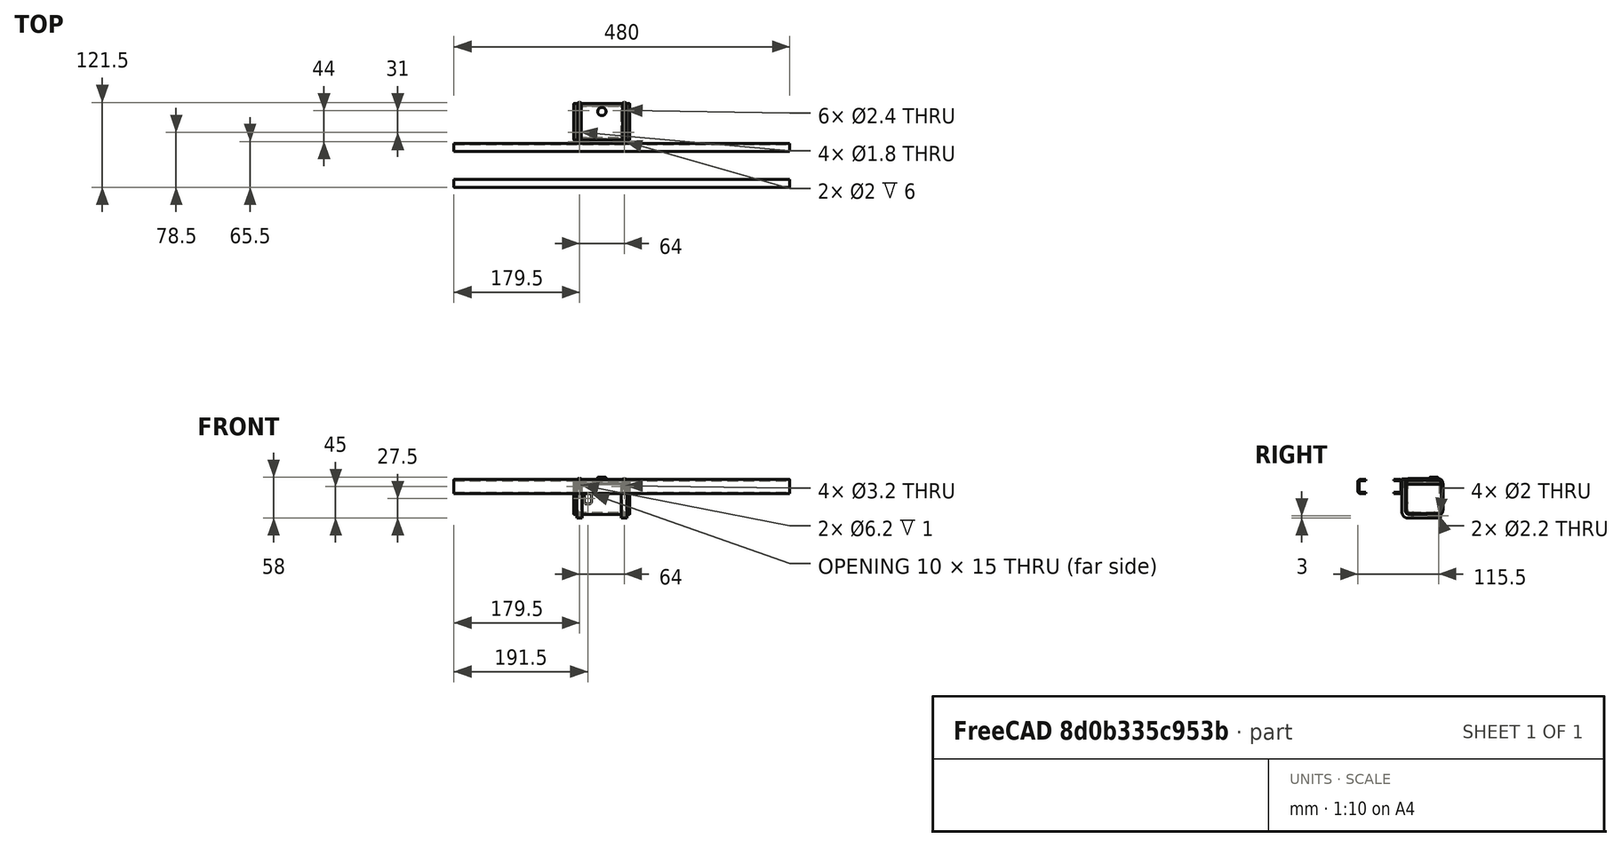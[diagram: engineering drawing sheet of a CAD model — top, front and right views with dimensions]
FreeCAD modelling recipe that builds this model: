
FCSTD DOCUMENT  (FreeCAD 0.16R5602 (Git))
Label: fuel-tank
License: All rights reserved
LicenseURL: http://en.wikipedia.org/wiki/All_rights_reserved
objects: Part::Box×35, Part::Cylinder×30, Part::Cut×27, Part::Fillet×26, Part::MultiFuse×19, Part::Chamfer×5, Part::Mirroring×1
note: 143 computed .brp shape members not serialized (recipe doc carries the construction recipe); baked Part::Feature solids carry a one-line shape summary decoded from their .brp

FEATURE [Part::Box] Box416  label="Cube641"
  Height = 20
  Length = 480
  Placement = pos=(0,0,-92) rot=(0,0,1;0rad)
  Width = 11.5
FEATURE [Part::Box] Box417  label="Cube642"
  Height = 17
  Length = 480
  Placement = pos=(0,1.5,-90.5) rot=(0,0,1;0rad)
  Width = 10
FEATURE [Part::Cut] Cut429  label="Cut769"
  Base = -> Box416
  Tool = -> Box417
FEATURE [Part::Fillet] Fillet268
  Base = -> Cut429
  Edges = 2 edges r=3: [Edge11,Edge23]
  Placement = pos=(0,-1.5,0) rot=(0,0,1;0rad)
FEATURE [Part::Box] Box418  label="Cube643"
  Height = 20
  Length = 480
  Placement = pos=(0,0,-92) rot=(0,0,1;0rad)
  Width = 11.5
FEATURE [Part::Box] Box419  label="Cube644"
  Height = 17
  Length = 480
  Placement = pos=(0,1.5,-90.5) rot=(0,0,1;0rad)
  Width = 10
FEATURE [Part::Cut] Cut430  label="Cut770"
  Base = -> Box418
  Tool = -> Box419
FEATURE [Part::Fillet] Fillet269
  Base = -> Cut430
  Edges = 2 edges r=3: [Edge11,Edge23]
FEATURE [Part::Mirroring] Part__Mirroring036  label="Fillet269 (Mirror #29)"
  Base = (0,0,0)
  Normal = (0,1,0)
  Placement = pos=(0,61.5,0) rot=(0,0,1;0rad)
  Source = -> Fillet269
FEATURE [Part::MultiFuse] Fusion231  label="frame-00"
  Placement = pos=(23.5,55,74) rot=(0,0,1;0rad)
  Shapes = -> [Part__Mirroring036,Fillet268]
FEATURE [Part::Box] Box517  label="Cube719"
  Height = 49
  Length = 0.5
  Placement = pos=(195,122,-50.5) rot=(0,0,1;0rad)
  Width = 51
FEATURE [Part::Fillet] Fillet372
  Base = -> Box517
  Edges = 4 edges r=6: [Edge9,Edge10,Edge11,Edge12]
FEATURE [Part::Cylinder] Cylinder950  label="Cylinder1002"
  Angle = 360
  Height = 2
  Placement = pos=(235,162,0) rot=(0,0,1;0rad)
  Radius = 6
FEATURE [Part::Cylinder] Cylinder951  label="Cylinder1003"
  Angle = 360
  Height = 3
  Placement = pos=(235,162,-1) rot=(0,0,1;0rad)
  Radius = 5
FEATURE [Part::MultiFuse] Fusion605
  Shapes = -> [Cylinder950,Cylinder951]
FEATURE [Part::Fillet] Fillet373
  Base = -> Fusion605
  Edges = 2 edges r=0.5: [Edge1,Edge3]
FEATURE [Part::Chamfer] Chamfer109
  Base = -> Fillet373
  Edges = 1 edges r=0.49: [Edge8]
FEATURE [Part::Box] Box518  label="Cube720"
  Height = 50
  Length = 80
  Placement = pos=(195,121.5,-51) rot=(0,0,1;0rad)
  Width = 52
FEATURE [Part::Fillet] Fillet374
  Base = -> Box518
  Edges = 4 edges r=6: [Edge9,Edge10,Edge11,Edge12]
FEATURE [Part::Box] Box519  label="Cube721"
  Height = 49
  Length = 0.5
  Placement = pos=(195,122,-50.5) rot=(0,0,1;0rad)
  Width = 51
FEATURE [Part::Fillet] Fillet375
  Base = -> Box519
  Edges = 4 edges r=6: [Edge9,Edge10,Edge11,Edge12]
  Placement = pos=(79.5,0,0) rot=(0,0,1;0rad)
FEATURE [Part::MultiFuse] Fusion606
  Shapes = -> [Chamfer109,Fillet374]
FEATURE [Part::MultiFuse] Fusion607
  Shapes = -> [Fillet375,Fillet372]
FEATURE [Part::Cut] Cut014115  label="Cut014173"
  Base = -> Fusion606
  Tool = -> Fusion607
FEATURE [Part::Chamfer] Chamfer110
  Base = -> Cut014115
  Edges = 2 edges r=0.49: [Edge59,Edge78]
FEATURE [Part::Fillet] Fillet376  label="_tank-00"
  Base = -> Chamfer110
  Edges = 2 edges r=0.49: [Edge15,Edge48]
FEATURE [Part::Box] Box523  label="Cube724"
  Height = 5
  Length = 8
  Placement = pos=(199,116.5,-53) rot=(0,0,1;0rad)
  Width = 55
FEATURE [Part::Box] Box527  label="Cube728"
  Height = 4
  Length = 5.5
  Placement = pos=(200.25,165.5,-52) rot=(0,0,1;0rad)
  Width = 6
FEATURE [Part::Cylinder] Cylinder954  label="Cylinder1006"
  Angle = 360
  Height = 8
  Placement = pos=(199,169,-50) rot=(0,1,0;1.5708rad)
  Radius = 1
FEATURE [Part::Box] Box539  label="Cube740"
  Height = 50
  Length = 8
  Placement = pos=(199,116.5,-48) rot=(0,0,1;0rad)
  Width = 5
FEATURE [Part::Box] Box540  label="Cube741"
  Height = 2.5
  Length = 5.5
  Placement = pos=(200.25,116.5,-0.5) rot=(0,0,1;0rad)
  Width = 5
FEATURE [Part::Cylinder] Cylinder962  label="Cylinder1013"
  Angle = 360
  Height = 10
  Placement = pos=(203,119,-6.5) rot=(0,0,1;0rad)
  Radius = 1
FEATURE [Part::Box] Box541  label="Cube742"
  Height = 44
  Length = 74
  Placement = pos=(198,124.5,-48) rot=(0,0,1;0rad)
  Width = 46
FEATURE [Part::Cylinder] Cylinder964  label="Cylinder1015"
  Angle = 360
  Height = 15
  Placement = pos=(203,123,-8) rot=(1,0,0;1.5708rad)
  Radius = 1.6
FEATURE [Part::Cylinder] Cylinder965  label="Cylinder1016"
  Angle = 360
  Height = 15
  Placement = pos=(267,123,-8) rot=(1,0,0;1.5708rad)
  Radius = 1.6
FEATURE [Part::Cylinder] Cylinder966  label="Cylinder1017"
  Angle = 360
  Height = 2
  Placement = pos=(203,123,-8) rot=(1,0,0;1.5708rad)
  Radius = 3.1
FEATURE [Part::Cylinder] Cylinder967  label="Cylinder1018"
  Angle = 360
  Height = 2
  Placement = pos=(267,123,-8) rot=(1,0,0;1.5708rad)
  Radius = 3.1
FEATURE [Part::MultiFuse] Fusion624
  Placement = pos=(0,2.5,0) rot=(0,0,1;0rad)
  Shapes = -> [Cylinder964,Cylinder966,Cylinder967,Cylinder965]
FEATURE [Part::Box] Box554  label="Cube755"
  Height = 15
  Length = 10
  Placement = pos=(210,118.5,-33) rot=(0,0,1;0rad)
  Width = 5
FEATURE [Part::Fillet] Fillet388
  Base = -> Box554
  Edges = 4 edges r=3: [Edge2,Edge4,Edge6,Edge8]
  Placement = pos=(0,1,0) rot=(0,0,1;0rad)
FEATURE [Part::Box] Box558  label="Cube759"
  Height = 44
  Length = 80
  Placement = pos=(195,121.5,-52) rot=(0,0,1;0rad)
  Width = 52
FEATURE [Part::Box] Box559  label="Cube760"
  Height = 10
  Length = 80
  Placement = pos=(195,121.5,-8) rot=(0,0,1;0rad)
  Width = 52
FEATURE [Part::Fillet] Fillet
  Base = -> Box541
  Edges = 4 edges r=4: [Edge9,Edge10,Edge11,Edge12]
FEATURE [Part::Cut] Cut  label="tank-lower"
  Base = -> Fillet376
  Tool = -> Fillet
FEATURE [Part::Box] Box560  label="Cube761"
  Height = 49
  Length = 0.5
  Placement = pos=(195,122,-50.5) rot=(0,0,1;0rad)
  Width = 51
FEATURE [Part::Fillet] Fillet390
  Base = -> Box560
  Edges = 4 edges r=6: [Edge9,Edge10,Edge11,Edge12]
FEATURE [Part::Cylinder] Cylinder971  label="Cylinder1022"
  Angle = 360
  Height = 2
  Placement = pos=(235,162,0) rot=(0,0,1;0rad)
  Radius = 6
FEATURE [Part::Cylinder] Cylinder972  label="Cylinder1023"
  Angle = 360
  Height = 3
  Placement = pos=(235,162,-1) rot=(0,0,1;0rad)
  Radius = 5
FEATURE [Part::MultiFuse] Fusion630
  Shapes = -> [Cylinder971,Cylinder972]
FEATURE [Part::Fillet] Fillet391
  Base = -> Fusion630
  Edges = 2 edges r=0.5: [Edge1,Edge3]
FEATURE [Part::Chamfer] Chamfer117
  Base = -> Fillet391
  Edges = 1 edges r=0.49: [Edge8]
FEATURE [Part::Box] Box561  label="Cube762"
  Height = 50
  Length = 80
  Placement = pos=(195,121.5,-51) rot=(0,0,1;0rad)
  Width = 52
FEATURE [Part::Fillet] Fillet392
  Base = -> Box561
  Edges = 4 edges r=6: [Edge9,Edge10,Edge11,Edge12]
FEATURE [Part::Box] Box562  label="Cube763"
  Height = 49
  Length = 0.5
  Placement = pos=(195,122,-50.5) rot=(0,0,1;0rad)
  Width = 51
FEATURE [Part::Fillet] Fillet393
  Base = -> Box562
  Edges = 4 edges r=6: [Edge9,Edge10,Edge11,Edge12]
  Placement = pos=(79.5,0,0) rot=(0,0,1;0rad)
FEATURE [Part::MultiFuse] Fusion631
  Shapes = -> [Chamfer117,Fillet392]
FEATURE [Part::MultiFuse] Fusion632
  Shapes = -> [Fillet393,Fillet390]
FEATURE [Part::Cut] Cut014136  label="Cut014168"
  Base = -> Fusion631
  Tool = -> Fusion632
FEATURE [Part::Chamfer] Chamfer118
  Base = -> Cut014136
  Edges = 2 edges r=0.49: [Edge59,Edge78]
FEATURE [Part::Fillet] Fillet394  label="_tank-001"
  Base = -> Chamfer118
  Edges = 2 edges r=0.49: [Edge15,Edge48]
FEATURE [Part::Box] Box563  label="Cube764"
  Height = 44
  Length = 74
  Placement = pos=(198,124.5,-48) rot=(0,0,1;0rad)
  Width = 46
FEATURE [Part::Fillet] Fillet395
  Base = -> Box563
  Edges = 4 edges r=4: [Edge9,Edge10,Edge11,Edge12]
FEATURE [Part::Cut] Cut014137  label="tank_upper"
  Base = -> Fillet394
  Tool = -> Fillet395
FEATURE [Part::Cut] Cut014138
  Base = -> Cut014137
  Placement = pos=(0,0,3) rot=(0,0,1;0rad)
  Tool = -> Box558
FEATURE [Part::Cut] Cut014139
  Base = -> Cut
  Placement = pos=(0,0,3) rot=(0,0,1;0rad)
  Tool = -> Box559
FEATURE [Part::Cut] Cut014140
  Base = -> Cut014139
  Tool = -> Fillet388
FEATURE [Part::Box] Box564  label="Cube765"
  Height = 2
  Length = 76
  Placement = pos=(197,123.5,-5) rot=(0,0,1;0rad)
  Width = 48
FEATURE [Part::Box] Box565  label="Cube766"
  Height = 2
  Length = 74
  Placement = pos=(198,124.5,-5) rot=(0,0,1;0rad)
  Width = 46
FEATURE [Part::Cut] Cut014141
  Base = -> Box564
  Tool = -> Box565
FEATURE [Part::Box] Box566  label="Cube767"
  Height = 2
  Length = 77
  Placement = pos=(196.5,123,-5) rot=(0,0,1;0rad)
  Width = 49
FEATURE [Part::Box] Box567  label="Cube768"
  Height = 2
  Length = 72
  Placement = pos=(199,125.5,-5) rot=(0,0,1;0rad)
  Width = 44
FEATURE [Part::Cut] Cut014142
  Base = -> Box566
  Tool = -> Box567
FEATURE [Part::Fillet] Fillet396
  Base = -> Cut014142
  Edges = 4 edges r=2.5: [Edge1,Edge3,Edge6,Edge15]
FEATURE [Part::Fillet] Fillet397
  Base = -> Cut014141
  Edges = 4 edges r=2: [Edge1,Edge3,Edge6,Edge15]
FEATURE [Part::MultiFuse] Fusion  label="_tank-lower-03"
  Shapes = -> [Cut014140,Fillet397]
FEATURE [Part::Cut] Cut014143  label="fuel-tank-upper"
  Base = -> Cut014138
  Tool = -> Fillet396
FEATURE [Part::Cylinder] Cylinder973  label="Cylinder1024"
  Angle = 360
  Height = 15
  Placement = pos=(203,123,-8) rot=(1,0,0;1.5708rad)
  Radius = 1.6
FEATURE [Part::Cut] Cut014148  label="_tank-lower-04"
  Base = -> Fusion
  Tool = -> Fusion624
FEATURE [Part::Cylinder] Cylinder975  label="Cylinder1026"
  Angle = 360
  Height = 15
  Placement = pos=(203,132,-59) rot=(0,0,1;0rad)
  Radius = 1.2
FEATURE [Part::Cylinder] Cylinder976  label="Cylinder1027"
  Angle = 360
  Height = 15
  Placement = pos=(203,163,-59) rot=(0,0,1;0rad)
  Radius = 1.2
FEATURE [Part::Cylinder] Cylinder977  label="Cylinder1028"
  Angle = 360
  Height = 15
  Placement = pos=(267,163,-59) rot=(0,0,1;0rad)
  Radius = 1.2
FEATURE [Part::Cylinder] Cylinder978  label="Cylinder1029"
  Angle = 360
  Height = 15
  Placement = pos=(267,132,-59) rot=(0,0,1;0rad)
  Radius = 1.2
FEATURE [Part::MultiFuse] Fusion637
  Shapes = -> [Cylinder975,Cylinder978,Cylinder976,Cylinder977]
FEATURE [Part::Cylinder] Cylinder979  label="Cylinder1030"
  Angle = 360
  Height = 15
  Placement = pos=(203,132,-59) rot=(0,0,1;0rad)
  Radius = 0.9
FEATURE [Part::Cylinder] Cylinder980  label="Cylinder1031"
  Angle = 360
  Height = 15
  Placement = pos=(203,163,-59) rot=(0,0,1;0rad)
  Radius = 0.9
FEATURE [Part::Cut] Cut014149  label="_tank-lower-05"
  Base = -> Cut014148
  Tool = -> Fusion637
FEATURE [Part::Cylinder] Cylinder983  label="Cylinder1034"
  Angle = 360
  Height = 15
  Placement = pos=(203,123,-8) rot=(1,0,0;1.5708rad)
  Radius = 3
FEATURE [Part::Cylinder] Cylinder984  label="Cylinder1035"
  Angle = 360
  Height = 15
  Placement = pos=(267,123,-8) rot=(1,0,0;1.5708rad)
  Radius = 3
FEATURE [Part::MultiFuse] Fusion640
  Placement = pos=(0,54,6) rot=(0,0,1;0rad)
  Shapes = -> [Cylinder983,Cylinder984]
FEATURE [Part::Cut] Cut014152  label="fuel-tank-lower"
  Base = -> Cut014149
  Tool = -> Fusion640
FEATURE [Part::Cut] Cut014157  label="Cut014174"
  Base = -> Box523
  Tool = -> Box527
FEATURE [Part::Cut] Cut014158  label="Cut014175"
  Base = -> Box539
  Tool = -> Box540
FEATURE [Part::MultiFuse] Fusion643
  Shapes = -> [Cylinder962,Cylinder954,Cylinder979,Cylinder980,Cylinder973]
FEATURE [Part::MultiFuse] Fusion644
  Shapes = -> [Cut014157,Cut014158]
FEATURE [Part::Cut] Cut014159  label="Cut014176"
  Base = -> Fusion644
  Tool = -> Fusion643
FEATURE [Part::Fillet] Fillet404
  Base = -> Cut014159
  Edges = 1 edges r=8: [Edge3]
FEATURE [Part::Fillet] Fillet405  label="fuel-tank-holder-front"
  Base = -> Fillet404
  Edges = 1 edges r=5: [Edge40]
FEATURE [Part::Box] Box570  label="Cube771"
  Height = 5
  Length = 8
  Placement = pos=(199,116.5,-53) rot=(0,0,1;0rad)
  Width = 55
FEATURE [Part::Box] Box571  label="Cube772"
  Height = 4
  Length = 5.5
  Placement = pos=(200.25,165.5,-52) rot=(0,0,1;0rad)
  Width = 6
FEATURE [Part::Cylinder] Cylinder985  label="Cylinder1036"
  Angle = 360
  Height = 8
  Placement = pos=(199,169,-50) rot=(0,1,0;1.5708rad)
  Radius = 1
FEATURE [Part::Box] Box572  label="Cube773"
  Height = 50
  Length = 8
  Placement = pos=(199,116.5,-48) rot=(0,0,1;0rad)
  Width = 5
FEATURE [Part::Box] Box573  label="Cube774"
  Height = 2.5
  Length = 5.5
  Placement = pos=(200.25,116.5,-0.5) rot=(0,0,1;0rad)
  Width = 5
FEATURE [Part::Cylinder] Cylinder986  label="Cylinder1037"
  Angle = 360
  Height = 10
  Placement = pos=(203,119,-6.5) rot=(0,0,1;0rad)
  Radius = 1
FEATURE [Part::Cylinder] Cylinder987  label="Cylinder1038"
  Angle = 360
  Height = 15
  Placement = pos=(203,123,-8) rot=(1,0,0;1.5708rad)
  Radius = 1.6
FEATURE [Part::Cylinder] Cylinder988  label="Cylinder1039"
  Angle = 360
  Height = 15
  Placement = pos=(203,132,-59) rot=(0,0,1;0rad)
  Radius = 0.9
FEATURE [Part::Cylinder] Cylinder989  label="Cylinder1040"
  Angle = 360
  Height = 15
  Placement = pos=(203,163,-59) rot=(0,0,1;0rad)
  Radius = 0.9
FEATURE [Part::Cut] Cut014160  label="Cut014180"
  Base = -> Box570
  Tool = -> Box571
FEATURE [Part::Cut] Cut014161  label="Cut014181"
  Base = -> Box572
  Tool = -> Box573
FEATURE [Part::MultiFuse] Fusion645
  Shapes = -> [Cylinder986,Cylinder985,Cylinder988,Cylinder989,Cylinder987]
FEATURE [Part::MultiFuse] Fusion646
  Shapes = -> [Cut014160,Cut014161]
FEATURE [Part::Cut] Cut014162  label="Cut014182"
  Base = -> Fusion646
  Tool = -> Fusion645
FEATURE [Part::Fillet] Fillet406
  Base = -> Cut014162
  Edges = 1 edges r=8: [Edge3]
FEATURE [Part::Fillet] Fillet407  label="fuel-tank-holder-rear"
  Base = -> Fillet406
  Edges = 1 edges r=5: [Edge40]
  Placement = pos=(64,0,0) rot=(0,0,1;0rad)
FEATURE [Part::Box] Box574  label="Cube775"
  Height = 52
  Length = 5
  Placement = pos=(201,120.5,-48) rot=(0,0,1;0rad)
  Width = 54
FEATURE [Part::Box] Box575  label="Cube776"
  Height = 50
  Length = 5
  Placement = pos=(201,121.5,-48) rot=(0,0,1;0rad)
  Width = 52
FEATURE [Part::Box] Box576  label="Cube777"
  Height = 50
  Length = 5
  Placement = pos=(201,117.5,-50) rot=(0,0,1;0rad)
  Width = 51
FEATURE [Part::Fillet] Fillet408
  Base = -> Box575
  Edges = 4 edges r=6: [Edge9,Edge10,Edge11,Edge12]
FEATURE [Part::Fillet] Fillet409
  Base = -> Box574
  Edges = 4 edges r=7: [Edge9,Edge10,Edge11,Edge12]
  Placement = pos=(0,0,-1) rot=(0,0,1;0rad)
FEATURE [Part::Cylinder] Cylinder990  label="Cylinder1041"
  Angle = 360
  Height = 5
  Placement = pos=(201,169,-50) rot=(0,1,0;1.5708rad)
  Radius = 2
FEATURE [Part::Cylinder] Cylinder991  label="Cylinder1042"
  Angle = 360
  Height = 5
  Placement = pos=(201,169,-50) rot=(0,1,0;1.5708rad)
  Radius = 1.1
FEATURE [Part::Box] Box577  label="Cube778"
  Height = 2.5
  Length = 5
  Placement = pos=(201,116.5,0) rot=(0,0,1;0rad)
  Width = 10
FEATURE [Part::Cylinder] Cylinder992  label="Cylinder1043"
  Angle = 360
  Height = 10
  Placement = pos=(203.5,119,-7.5) rot=(0,0,1;0rad)
  Radius = 1.2
FEATURE [Part::Cut] Cut014170  label="Cut014184"
  Base = -> Fillet409
  Tool = -> Box576
FEATURE [Part::MultiFuse] Fusion649
  Shapes = -> [Cut014170,Box577,Cylinder990]
FEATURE [Part::Cut] Cut014171
  Base = -> Fusion649
  Placement = pos=(-0.5,0,0) rot=(0,0,1;0rad)
  Tool = -> Fillet408
FEATURE [Part::MultiFuse] Fusion650
  Placement = pos=(-0.5,0,0) rot=(0,0,1;0rad)
  Shapes = -> [Cylinder991,Cylinder992]
FEATURE [Part::Cut] Cut014172
  Base = -> Cut014171
  Tool = -> Fusion650
FEATURE [Part::Chamfer] Chamfer119  label="fuel-tank-lace-rear"
  Base = -> Cut014172
  Edges = 1 edges r=0.145: [Edge4]
  Placement = pos=(64,0,0) rot=(0,0,1;0rad)
FEATURE [Part::Box] Box578  label="Cube779"
  Height = 53
  Length = 5
  Placement = pos=(200.5,120,-48.5) rot=(0,0,1;0rad)
  Width = 55
FEATURE [Part::Box] Box579  label="Cube780"
  Height = 51
  Length = 5
  Placement = pos=(200.5,121,-48.5) rot=(0,0,1;0rad)
  Width = 53
FEATURE [Part::Box] Box580  label="Cube781"
  Height = 50
  Length = 5
  Placement = pos=(200.5,117.5,-50) rot=(0,0,1;0rad)
  Width = 51
FEATURE [Part::Fillet] Fillet410
  Base = -> Box579
  Edges = 4 edges r=6.5: [Edge9,Edge10,Edge11,Edge12]
FEATURE [Part::Fillet] Fillet411
  Base = -> Box578
  Edges = 4 edges r=7.5: [Edge9,Edge10,Edge11,Edge12]
  Placement = pos=(0,0,-1) rot=(0,0,1;0rad)
FEATURE [Part::Cylinder] Cylinder993  label="Cylinder1044"
  Angle = 360
  Height = 5
  Placement = pos=(200.5,169,-50) rot=(0,1,0;1.5708rad)
  Radius = 2
FEATURE [Part::Cylinder] Cylinder994  label="Cylinder1045"
  Angle = 360
  Height = 5
  Placement = pos=(201,169,-50) rot=(0,1,0;1.5708rad)
  Radius = 1.1
FEATURE [Part::Box] Box581  label="Cube782"
  Height = 2.5
  Length = 5
  Placement = pos=(200.5,116.5,0) rot=(0,0,1;0rad)
  Width = 10
FEATURE [Part::Cylinder] Cylinder995  label="Cylinder1046"
  Angle = 360
  Height = 10
  Placement = pos=(203.5,119,-7.5) rot=(0,0,1;0rad)
  Radius = 1.2
FEATURE [Part::MultiFuse] Fusion652
  Placement = pos=(-0.5,0,0) rot=(0,0,1;0rad)
  Shapes = -> [Cylinder994,Cylinder995]
FEATURE [Part::Cut] Cut014173  label="Cut014185"
  Base = -> Fillet411
  Tool = -> Box580
FEATURE [Part::MultiFuse] Fusion653
  Shapes = -> [Cut014173,Cylinder993,Box581]
FEATURE [Part::Cut] Cut014174  label="Cut014186"
  Base = -> Fusion653
  Tool = -> Fillet410
FEATURE [Part::Cut] Cut014175  label="Cut014187"
  Base = -> Cut014174
  Tool = -> Fusion652
FEATURE [Part::Fillet] Fillet412  label="fuel-tank-lace-front"
  Base = -> Cut014175
  Edges = 2 edges r=1.5: [Edge26,Edge45]
